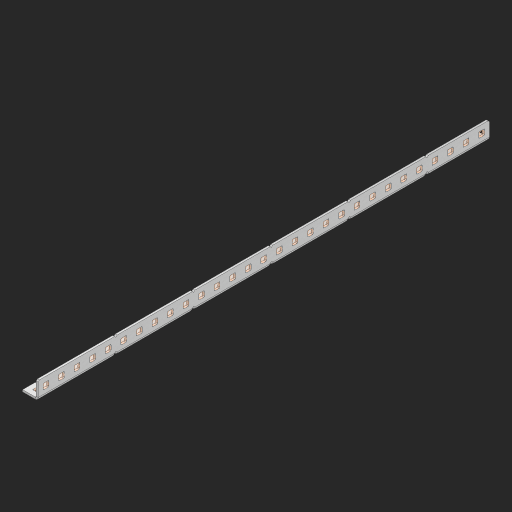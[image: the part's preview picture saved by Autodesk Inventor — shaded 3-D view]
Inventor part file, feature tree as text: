
AUTODESK INVENTOR PART (.ipt)
format: ipt  version: 2023 (Build 270158000, 158)  size: 1,220,096 bytes
history: native  units: in
note: dims shown in document units (in); Inventor stores cm internally (conversion verified against a paired STEP export)
features: other x235, extrude x85, sheet_metal_op x11, sketch x10, pattern_linear x2, mirror x1, chamfer x1
ambient origin geometry x8: Origin, YZ Plane, XZ Plane, XY Plane, X Axis, Y Axis, Z Axis, Center Point
bodies: Solid1 (feature_tree), Body (feature_tree)
feature tree (345):
  other  "Alu Half C 1x2x1x29"
  other  "Table"
  other  "Alu C 1x2x1x35"
  other  "Alu C 1x2x1x34"
  other  "Alu C 1x2x1x33"
  other  "Alu C 1x2x1x32"
  other  "Alu C 1x2x1x31"
  other  "Alu C 1x2x1x30"
  other  "Alu C 1x2x1x29"
  other  "Alu C 1x2x1x28"
  other  "Alu C 1x2x1x27"
  other  "Alu C 1x2x1x26"
  other  "Alu C 1x2x1x25"
  other  "Alu C 1x2x1x24"
  other  "Alu C 1x2x1x23"
  other  "Alu C 1x2x1x22"
  other  "Alu C 1x2x1x21"
  other  "Alu C 1x2x1x20"
  other  "Alu C 1x2x1x19"
  other  "Alu C 1x2x1x18"
  other  "Alu C 1x2x1x17"
  other  "Alu C 1x2x1x16"
  other  "Alu C 1x2x1x15"
  other  "Alu C 1x2x1x14"
  other  "Alu C 1x2x1x13"
  other  "Alu C 1x2x1x12"
  other  "Alu C 1x2x1x11"
  other  "Alu C 1x2x1x10"
  other  "Alu C 1x2x1x9"
  other  "Alu C 1x2x1x8"
  other  "Alu C 1x2x1x7"
  other  "Alu C 1x2x1x6"
  other  "Alu C 1x2x1x5"
  other  "Alu C 1x2x1x4"
  other  "Alu C 1x2x1x3"
  other  "Alu C 1x2x1x2"
  other  "Alu C 1x2x1x1"
  other  "Steel C 1x2x1x35"
  other  "Steel C 1x2x1x34"
  other  "Steel C 1x2x1x33"
  other  "Steel C 1x2x1x32"
  other  "Steel C 1x2x1x31"
  other  "Steel C 1x2x1x30"
  other  "Steel C 1x2x1x29"
  other  "Steel C 1x2x1x28"
  other  "Steel C 1x2x1x27"
  other  "Steel C 1x2x1x26"
  other  "Steel C 1x2x1x25"
  other  "Steel C 1x2x1x24"
  other  "Steel C 1x2x1x23"
  other  "Steel C 1x2x1x22"
  other  "Steel C 1x2x1x21"
  other  "Steel C 1x2x1x20"
  other  "Steel C 1x2x1x19"
  other  "Steel C 1x2x1x18"
  other  "Steel C 1x2x1x17"
  other  "Steel C 1x2x1x16"
  other  "Steel C 1x2x1x15"
  other  "Steel C 1x2x1x14"
  other  "Steel C 1x2x1x13"
  other  "Steel C 1x2x1x12"
  other  "Steel C 1x2x1x11"
  other  "Steel C 1x2x1x10"
  other  "Steel C 1x2x1x9"
  other  "Steel C 1x2x1x8"
  other  "Steel C 1x2x1x7"
  other  "Steel C 1x2x1x6"
  other  "Steel C 1x2x1x5"
  other  "Steel C 1x2x1x4"
  other  "Steel C 1x2x1x3"
  other  "Steel C 1x2x1x2"
  other  "Steel C 1x2x1x1"
  other  "Alu Half C 1x2x1x35"
  other  "Alu Half C 1x2x1x34"
  other  "Alu Half C 1x2x1x33"
  other  "Alu Half C 1x2x1x32"
  other  "Alu Half C 1x2x1x31"
  other  "Alu Half C 1x2x1x30"
  other  "Alu Half C 1x2x1x28"
  other  "Alu Half C 1x2x1x27"
  other  "Alu Half C 1x2x1x26"
  other  "Alu Half C 1x2x1x25"
  other  "Alu Half C 1x2x1x24"
  other  "Alu Half C 1x2x1x23"
  other  "Alu Half C 1x2x1x22"
  other  "Alu Half C 1x2x1x21"
  other  "Alu Half C 1x2x1x20"
  other  "Alu Half C 1x2x1x19"
  other  "Alu Half C 1x2x1x18"
  other  "Alu Half C 1x2x1x17"
  other  "Alu Half C 1x2x1x16"
  other  "Alu Half C 1x2x1x15"
  other  "Alu Half C 1x2x1x14"
  other  "Alu Half C 1x2x1x13"
  other  "Alu Half C 1x2x1x12"
  other  "Alu Half C 1x2x1x11"
  other  "Alu Half C 1x2x1x10"
  other  "Alu Half C 1x2x1x9"
  other  "Alu Half C 1x2x1x8"
  other  "Alu Half C 1x2x1x7"
  other  "Alu Half C 1x2x1x6"
  other  "Alu Half C 1x2x1x5"
  other  "Alu Half C 1x2x1x4"
  other  "Alu Half C 1x2x1x3"
  other  "Alu Half C 1x2x1x2"
  other  "Alu Half C 1x2x1x1"
  other  "Steel Half C 1x2x1x35"
  other  "Steel Half C 1x2x1x34"
  other  "Steel Half C 1x2x1x33"
  other  "Steel Half C 1x2x1x32"
  other  "Steel Half C 1x2x1x31"
  other  "Steel Half C 1x2x1x30"
  other  "Steel Half C 1x2x1x29"
  other  "Steel Half C 1x2x1x28"
  other  "Steel Half C 1x2x1x27"
  other  "Steel Half C 1x2x1x26"
  other  "Steel Half C 1x2x1x25"
  other  "Steel Half C 1x2x1x24"
  other  "Steel Half C 1x2x1x23"
  other  "Steel Half C 1x2x1x22"
  other  "Steel Half C 1x2x1x21"
  other  "Steel Half C 1x2x1x20"
  other  "Steel Half C 1x2x1x19"
  other  "Steel Half C 1x2x1x18"
  other  "Steel Half C 1x2x1x17"
  other  "Steel Half C 1x2x1x16"
  other  "Steel Half C 1x2x1x15"
  other  "Steel Half C 1x2x1x14"
  other  "Steel Half C 1x2x1x13"
  other  "Steel Half C 1x2x1x12"
  other  "Steel Half C 1x2x1x11"
  other  "Steel Half C 1x2x1x10"
  other  "Steel Half C 1x2x1x9"
  other  "Steel Half C 1x2x1x8"
  other  "Steel Half C 1x2x1x7"
  other  "Steel Half C 1x2x1x6"
  other  "Steel Half C 1x2x1x5"
  other  "Steel Half C 1x2x1x4"
  other  "Steel Half C 1x2x1x3"
  other  "Steel Half C 1x2x1x2"
  other  "Steel Half C 1x2x1x1"
  sheet_metal_op  "Flanges"
  other  "Flange Pattern Plane"
  other  "Flange Pattern Sketch"
  sheet_metal_op  "Flange Pattern"
  sheet_metal_op  "Body Pattern"
  pattern_linear  "Center Pattern"  Spacing1=0.0625in  [1 undecoded]
  other  "Arc Length"
  mirror  "Notch Mirror"
  pattern_linear  "Notch Pattern"  Spacing1=0.182in  [1 undecoded]
  chamfer  "End Chamfer"
  extrude  "Half Cut"  Depth=0.02in
  sketch  "Sketch1"  dims[d0=1.0in]
  other  "Plate1"
  sketch  "Sketch2"  dims[d1=14.5in]
  other  "Plate2"
  sheet_metal_op  "Bend1"
  sheet_metal_op  "Corner1"
  sketch  "Sketch3"  dims[d2=0.0625in]
  sketch  "Sketch7"  dims[d3=0.0625in]
  other  "Srf1"
  other  "Srf2"
  sketch  "Sketch8"  dims[d4=0.0312in]
  sketch  "Sketch9"  dims[d5=0.125in]
  other  "Srf91"
  sheet_metal_op  "Body Pattern Sketch"
  other  "Srf92"
  sketch  "Sketch13"  dims[d6=0.0625in]
  sketch  "Sketch14"  dims[d7=0.5in d8=90.0deg d9=0.0312in]
  sketch  "Sketch15"  dims[d10=0.25in]
  sketch  "Sketch16"  dims[d11=0.0625in d12=0.0625in d16=0.182in d17=0.02in d18=0.0625in d19=0.0in d20=0.25in d21=0.25in d38=11.4173in d40=0.5in d41=0.3937in d43=1.0in d46=0.172in d47=1.0in d48=0.0in d49=0.182in d50=0.02in d51=0.25in d52=0.25in d53=0.0625in d54=0.0in d55=0.172in d56=1.0in d57=0.0in d58=0.25in d60=11.4173in d62=0.5in d63=0.3937in d65=0.5in d85=0.1473in d86=0.1782in d88=0.04in d89=0.0625in d90=0.0in d91=0.04in d92=0.0491in d95=2.5in d96=0.04in d97=0.25in d98=45.0deg d99=0.25in d100=0.5in d101=0.0in d102=2.497in d106=0.182in d107=0.02in d108=0.5in d109=0.5in d110=0.0625in d111=0.0in d112=0.172in d113=0.5in d114=0.0in d117=0.5in d118=0.5in d119=0.5in]
  other  "Srf786"
  other  "Srf823"
  other  "Srf824"
  other  "Srf825"
  other  "Srf826"
  other  "Srf827"
  other  "Srf828"
  other  "Srf829"
  other  "Srf856"
  other  "Srf857"
  other  "Srf858"
  other  "Srf859"
  other  "Srf860"
  other  "Srf861"
  other  "Srf862"
  other  "Srf889"
  other  "Srf890"
  other  "Srf891"
  other  "Srf892"
  other  "Srf893"
  other  "Srf894"
  other  "Srf895"
  other  "Srf896"
  other  "Srf922"
  other  "Srf923"
  other  "Srf924"
  other  "Srf925"
  other  "Srf926"
  other  "Srf959"
  other  "Srf960"
  other  "Srf961"
  other  "Srf962"
  other  "Srf963"
  other  "Srf996"
  other  "Srf997"
  other  "Srf998"
  other  "Srf999"
  other  "Srf1000"
  other  "Srf1143"
  other  "Srf1144"
  other  "Srf1145"
  other  "Srf1146"
  other  "Srf1147"
  other  "Srf1148"
  other  "Srf1149"
  other  "Srf1150"
  other  "Srf1151"
  other  "Srf1152"
  other  "Srf1153"
  other  "Srf1154"
  other  "Srf1155"
  other  "Srf1156"
  other  "Srf1157"
  other  "Srf1199"
  other  "Srf1200"
  other  "Srf1201"
  other  "Srf1202"
  other  "Srf1203"
  other  "Srf1204"
  other  "Srf1205"
  other  "Srf1206"
  other  "Srf1207"
  other  "Srf1208"
  other  "Srf1209"
  other  "Srf1210"
  other  "Srf1211"
  other  "Srf1212"
  other  "Srf1213"
  other  "Srf1255"
  other  "Srf1256"
  other  "Srf1257"
  other  "Srf1258"
  other  "Srf1259"
  other  "Srf1260"
  other  "Srf1261"
  other  "Srf1262"
  other  "Srf1263"
  other  "Srf1264"
  other  "Srf1265"
  other  "Srf1266"
  other  "Srf1267"
  other  "Srf1268"
  other  "Srf1269"
  sheet_metal_op  "Flange Stamp"
  sheet_metal_op  "Flange Circle"
  sheet_metal_op  "Body Stamp"
  sheet_metal_op  "Body Circle"
  other  "Center Stamp"
  other  "Center Circle"
  sheet_metal_op  "Notch"
  extrude  "ExtrusionSrf2"  Depth=0.0625in
  extrude  "ExtrusionSrf92"  TaperAngle=0.0deg  [1 undecoded]
  extrude  "ExtrusionSrf823"  Depth=0.5in
  extrude  "ExtrusionSrf824"  Depth=0.5in
  extrude  "ExtrusionSrf825"  Depth=0.5in
  extrude  "ExtrusionSrf826"  Depth=0.5in
  extrude  "ExtrusionSrf827"  Depth=1.0in TaperAngle=0.0deg
  extrude  "ExtrusionSrf828"  Depth=0.182in
  extrude  "ExtrusionSrf829"  Depth=0.02in
  extrude  "ExtrusionSrf856"  Depth=0.5in
  extrude  "ExtrusionSrf857"  Depth=0.5in
  extrude  "ExtrusionSrf858"  Depth=0.0625in
  extrude  "ExtrusionSrf859"  TaperAngle=0.0deg  [1 undecoded]
  extrude  "ExtrusionSrf860"  Depth=0.5in
  extrude  "ExtrusionSrf861"  Depth=1.0in TaperAngle=0.0deg
  extrude  "ExtrusionSrf862"  Depth=0.5in
  extrude  "ExtrusionSrf889"  Depth=0.5in
  extrude  "ExtrusionSrf890"  Depth=0.5in
  extrude  "ExtrusionSrf891"  Depth=0.5in
  extrude  "ExtrusionSrf892"  Depth=0.5in
  extrude  "ExtrusionSrf893"  Depth=0.5in
  extrude  "ExtrusionSrf894"  Depth=0.0625in
  extrude  "ExtrusionSrf895"  TaperAngle=0.0deg  [1 undecoded]
  extrude  "ExtrusionSrf896"  Depth=0.5in
  extrude  "ExtrusionSrf922"  Depth=0.5in
  extrude  "ExtrusionSrf923"  Depth=0.5in
  extrude  "ExtrusionSrf924"  Depth=0.5in TaperAngle=45.0deg
  extrude  "ExtrusionSrf925"  Depth=0.5in
  extrude  "ExtrusionSrf926"  Depth=0.5in TaperAngle=0.0deg
  extrude  "ExtrusionSrf959"  Depth=0.5in
  extrude  "ExtrusionSrf960"  Depth=0.182in
  extrude  "ExtrusionSrf961"  Depth=0.02in
  extrude  "ExtrusionSrf962"  Depth=0.5in
  extrude  "ExtrusionSrf963"  Depth=0.5in
  extrude  "ExtrusionSrf996"  Depth=0.0625in
  extrude  "ExtrusionSrf997"  TaperAngle=0.0deg  [1 undecoded]
  extrude  "ExtrusionSrf998"  Depth=0.5in
  extrude  "ExtrusionSrf999"  Depth=0.5in TaperAngle=0.0deg
  extrude  "ExtrusionSrf1000"  Depth=0.5in
  extrude  "ExtrusionSrf1143"  Depth=0.5in
  extrude  "ExtrusionSrf1144"  Depth=0.5in
  extrude  "ExtrusionSrf1145"  [1 undecoded]
  extrude  "ExtrusionSrf1146"  [1 undecoded]
  extrude  "ExtrusionSrf1147"  [1 undecoded]
  extrude  "ExtrusionSrf1148"  [1 undecoded]
  extrude  "ExtrusionSrf1149"  [1 undecoded]
  extrude  "ExtrusionSrf1150"  [1 undecoded]
  extrude  "ExtrusionSrf1151"  [1 undecoded]
  extrude  "ExtrusionSrf1152"  [1 undecoded]
  extrude  "ExtrusionSrf1153"  [1 undecoded]
  extrude  "ExtrusionSrf1154"  [1 undecoded]
  extrude  "ExtrusionSrf1155"  [1 undecoded]
  extrude  "ExtrusionSrf1156"  [1 undecoded]
  extrude  "ExtrusionSrf1157"  [1 undecoded]
  extrude  "ExtrusionSrf1199"  [1 undecoded]
  extrude  "ExtrusionSrf1200"  [1 undecoded]
  extrude  "ExtrusionSrf1201"  [1 undecoded]
  extrude  "ExtrusionSrf1202"  [1 undecoded]
  extrude  "ExtrusionSrf1203"  [1 undecoded]
  extrude  "ExtrusionSrf1204"  [1 undecoded]
  extrude  "ExtrusionSrf1205"  [1 undecoded]
  extrude  "ExtrusionSrf1206"  [1 undecoded]
  extrude  "ExtrusionSrf1207"  [1 undecoded]
  extrude  "ExtrusionSrf1208"  [1 undecoded]
  extrude  "ExtrusionSrf1209"  [1 undecoded]
  extrude  "ExtrusionSrf1210"  [1 undecoded]
  extrude  "ExtrusionSrf1211"  [1 undecoded]
  extrude  "ExtrusionSrf1212"  [1 undecoded]
  extrude  "ExtrusionSrf1213"  [1 undecoded]
  extrude  "ExtrusionSrf1255"  [1 undecoded]
  extrude  "ExtrusionSrf1256"  [1 undecoded]
  extrude  "ExtrusionSrf1257"  [1 undecoded]
  extrude  "ExtrusionSrf1258"  [1 undecoded]
  extrude  "ExtrusionSrf1259"  [1 undecoded]
  extrude  "ExtrusionSrf1260"  [1 undecoded]
  extrude  "ExtrusionSrf1261"  [1 undecoded]
  extrude  "ExtrusionSrf1262"  [1 undecoded]
  extrude  "ExtrusionSrf1263"  [1 undecoded]
  extrude  "ExtrusionSrf1264"  [1 undecoded]
  extrude  "ExtrusionSrf1265"  [1 undecoded]
  extrude  "ExtrusionSrf1266"  [1 undecoded]
  extrude  "ExtrusionSrf1267"  [1 undecoded]
  extrude  "ExtrusionSrf1268"  [1 undecoded]
  extrude  "ExtrusionSrf1269"  [1 undecoded]
note: 49 required parameter values undecoded (feature->parameter linkage not recoverable at this tier; creation-order binding heuristic only, values carry confidence <= 0.55)
